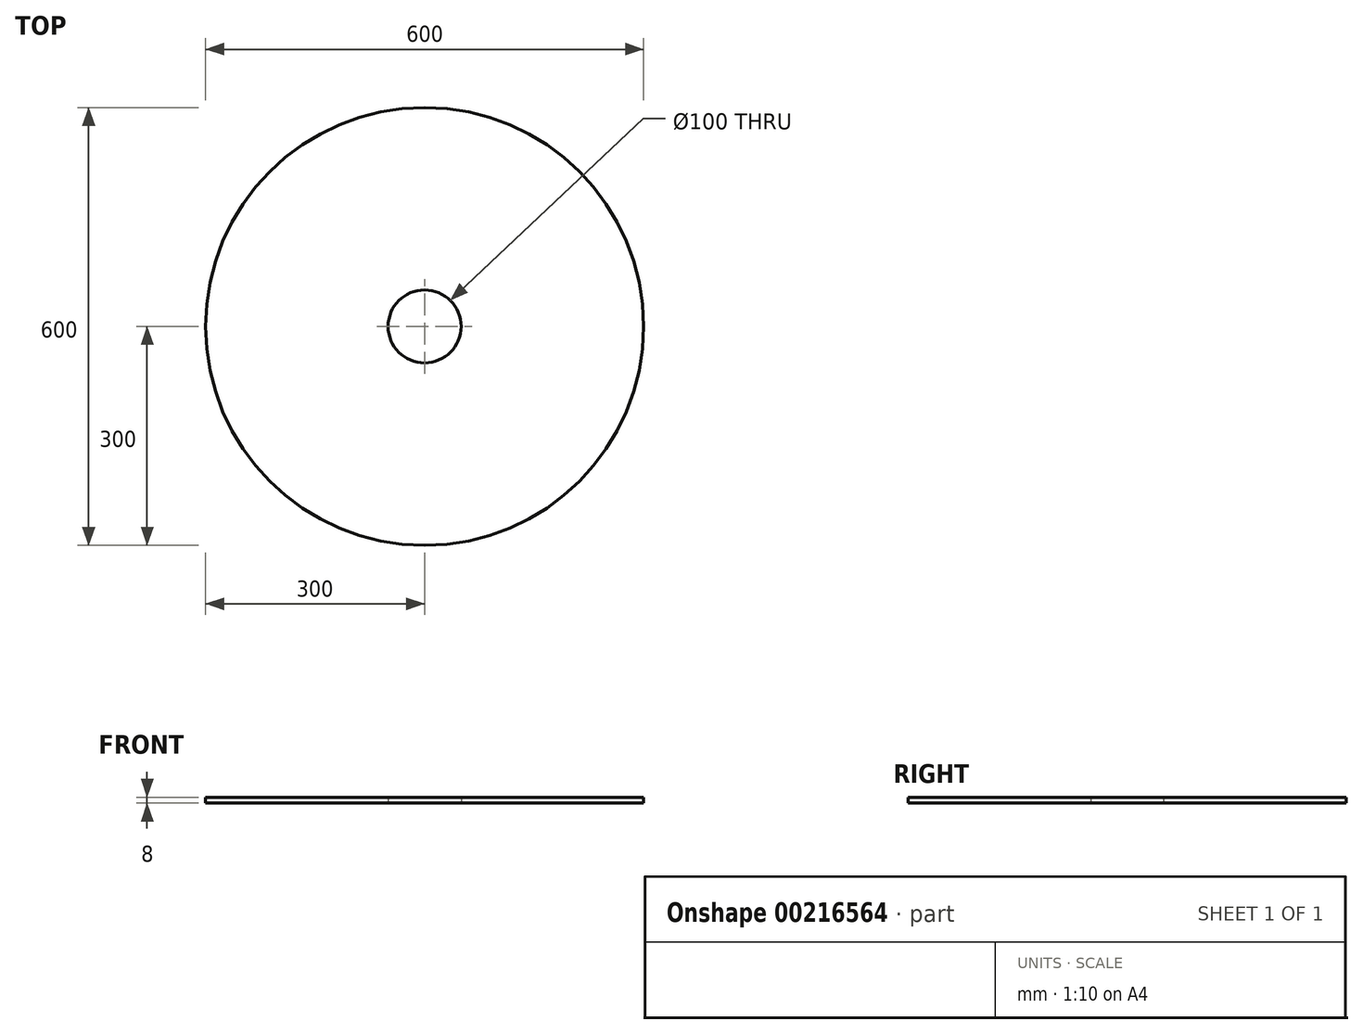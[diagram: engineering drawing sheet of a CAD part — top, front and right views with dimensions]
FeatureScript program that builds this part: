
annotation { "Feature Type Name" : "Feature", "Feature Type Description" : "" }
export const myFeature = defineFeature(function(context is Context, id is Id, definition is map)
    precondition{}
    {
        {
            var Q0;
            Q0=qCreatedBy(makeId("Top.planeOp"),FACE);
            var sketch = newSketch(context, id + "F0", { "sketchPlane" : qUnion([Q0])});
            skCircle(sketch, "E0", {"center": v(0, 0) * mm, "radius": 50 * mm});
            skCircle(sketch, "E1", {"center": v(0, 0) * mm, "radius": 300 * mm});
            skSolve(sketch);
        }
        {
            var Q0;
            Q0=makeQuery(id+"F0.imprint","IMPRINT",FACE,{"disambiguationData":[TD([[makeQuery(id+"F0.imprint","IMPRINT",EDGE,{"derivedFrom":sQuery(id+"F0.wireOp",EDGE,"E0")}),-1.0]])]});
            extrude(context, id + "F1", {"entities" : qUnion([Q0]), "depth" : 8 * mm});
        }
    });
